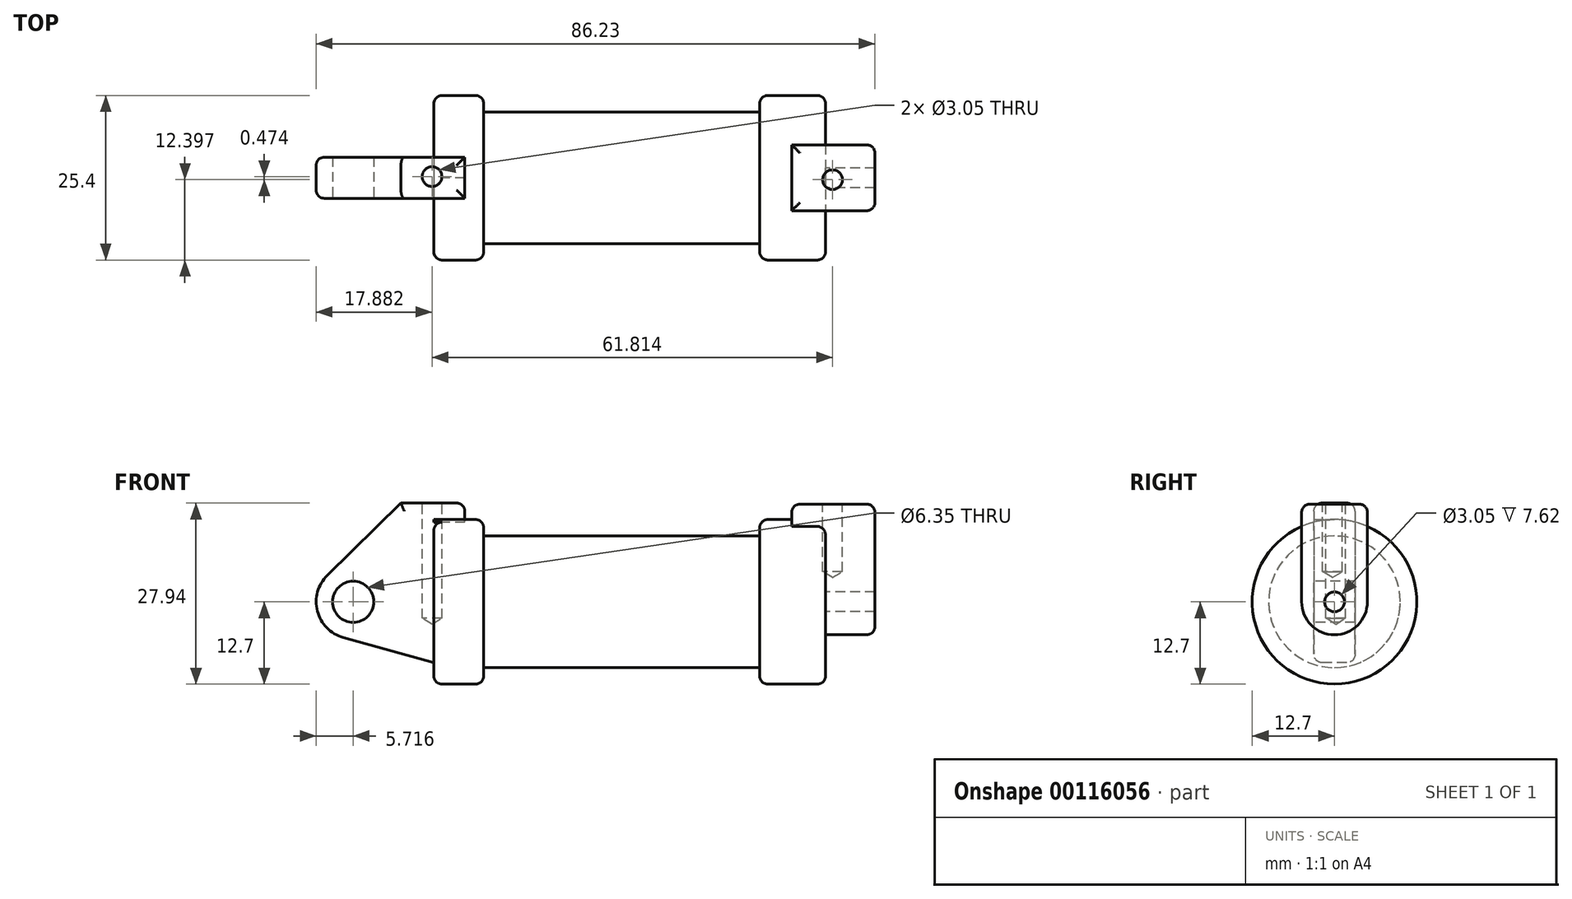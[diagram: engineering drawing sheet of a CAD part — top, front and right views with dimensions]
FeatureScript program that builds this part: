
annotation { "Feature Type Name" : "Feature", "Feature Type Description" : "" }
export const myFeature = defineFeature(function(context is Context, id is Id, definition is map)
    precondition{}
    {
        {
            var Q0;
            Q0=qCreatedBy(makeId("Front.planeOp"),FACE);
            var sketch = newSketch(context, id + "F0", { "sketchPlane" : qUnion([Q0])});
            skLineSegment(sketch, "E0", {"start": v(0, 0) * mm, "end": v(0, 12.7) * mm});
            skLineSegment(sketch, "E1", {"start": v(0, 12.7) * mm, "end": v(10.16, 12.7) * mm});
            skLineSegment(sketch, "E2", {"start": v(10.16, 12.7) * mm, "end": v(10.16, 10.16) * mm});
            skLineSegment(sketch, "E3", {"start": v(10.16, 10.16) * mm, "end": v(56.13, 10.16) * mm});
            skLineSegment(sketch, "E4", {"start": v(56.13, 10.16) * mm, "end": v(56.13, 12.7) * mm});
            skLineSegment(sketch, "E5", {"start": v(56.13, 12.7) * mm, "end": v(66.3, 12.7) * mm});
            skLineSegment(sketch, "E6", {"start": v(66.3, 12.7) * mm, "end": v(66.3, 0) * mm});
            skLineSegment(sketch, "E7", {"start": v(66.3, 0) * mm, "end": v(0, 0) * mm});
            skLineSegment(sketch, "E8", {"start": v(5.84, 15.24) * mm, "end": v(0.76, 15.24) * mm});
            skLineSegment(sketch, "E9", {"start": v(0.76, 15.24) * mm, "end": v(-10.6, 4.08) * mm});
            skLineSegment(sketch, "E10", {"start": v(0, 0) * mm, "end": v(-6.6, 0) * mm});
            skCircle(sketch, "E11", {"center": v(-6.6, 0) * mm, "radius": 5.72 * mm});
            skCircle(sketch, "E12", {"center": v(-6.6, 0) * mm, "radius": 3.18 * mm});
            skLineSegment(sketch, "E13", {"start": v(5.84, 15.24) * mm, "end": v(5.84, -9.4) * mm});
            skLineSegment(sketch, "E14", {"start": v(5.84, -9.4) * mm, "end": v(-8.14, -5.5) * mm});
            skSolve(sketch);
        }
        {
            var Q0;
            {var subQ0=sQuery(id+"F0.wireOp",EDGE,"E2");Q0=makeQuery(id+"F0.imprint","IMPRINT",FACE,{"disambiguationData":[TD([[makeQuery(id+"F0.imprint","IMPRINT",EDGE,{"derivedFrom":subQ0}),-1.0]])]});}
            var Q1;
            Q1=sQuery(id+"F0.wireOp",EDGE,"E7");
            revolve(context, id + "F1", {"entities" : qUnion([Q0]), "axis" : qUnion([Q1]), "revolveType" : RevolveType.FULL});
        }
        {
            var Q0;
            {var subQ0=sQuery(id+"F0.wireOp",EDGE,"E14");Q0=makeQuery(id+"F0.imprint","IMPRINT",FACE,{"disambiguationData":[TD([[makeQuery(id+"F0.imprint","IMPRINT",EDGE,{"derivedFrom":subQ0}),-1.0]])]});}
            var Q1;
            {var subQ0=sQuery(id+"F0.wireOp",EDGE,"E0");Q1=makeQuery(id+"F0.imprint","IMPRINT",FACE,{"disambiguationData":[TD([[makeQuery(id+"F0.imprint","IMPRINT",EDGE,{"derivedFrom":subQ0}),-1.0]])]});}
            var Q2;
            {var subQ4=sQuery(id+"F0.wireOp",EDGE,"E12");Q2=makeQuery(id+"F0.imprint","IMPRINT",FACE,{"disambiguationData":[TD([[makeQuery(id+"F0.imprint","IMPRINT",EDGE,{"derivedFrom":subQ4}),-1.0]])]});}
            var Q3;
            {var subQ3=sQuery(id+"F0.wireOp",EDGE,"E0");Q3=makeQuery(id+"F0.imprint","IMPRINT",FACE,{"disambiguationData":[TD([[makeQuery(id+"F0.imprint","IMPRINT",EDGE,{"derivedFrom":subQ3}),1.0]])]});}
            extrude(context, id + "F2", {"entities" : qUnion([Q0, Q1, Q2, Q3]), "operationType" : NewBodyOperationType.ADD, "oppositeDirection" : true, "depth" : 3.17 * mm});
        }
        {
            var Q0;
            {var subQ3=sQuery(id+"F0.wireOp",EDGE,"E0");Q0=makeQuery(id+"F0.imprint","IMPRINT",FACE,{"disambiguationData":[TD([[makeQuery(id+"F0.imprint","IMPRINT",EDGE,{"derivedFrom":subQ3}),1.0]])]});}
            var Q1;
            {var subQ0=sQuery(id+"F0.wireOp",EDGE,"E14");Q1=makeQuery(id+"F0.imprint","IMPRINT",FACE,{"disambiguationData":[TD([[makeQuery(id+"F0.imprint","IMPRINT",EDGE,{"derivedFrom":subQ0}),-1.0]])]});}
            var Q2;
            {var subQ4=sQuery(id+"F0.wireOp",EDGE,"E12");Q2=makeQuery(id+"F0.imprint","IMPRINT",FACE,{"disambiguationData":[TD([[makeQuery(id+"F0.imprint","IMPRINT",EDGE,{"derivedFrom":subQ4}),-1.0]])]});}
            extrude(context, id + "F3", {"entities" : qUnion([Q0, Q1, Q2]), "operationType" : NewBodyOperationType.ADD, "depth" : 3.17 * mm});
        }
        {
            var Q0;
            Q0=makeQuery(id+"F1.opRevolve","SWEPT_FACE",FACE,{"disambiguationData":[OSD([sQuery(id+"F0.wireOp",EDGE,"E2")])]});
            extrude(context, id + "F4", {"entities" : qUnion([Q0]), "operationType" : NewBodyOperationType.ADD, "depth" : 3.38 * mm});
        }
        {
            var Q0;
            {var subQ0=sQuery(id+"F0.wireOp",EDGE,"E13");Q0=makeQuery(id+"F3.boolean.opBoolean","MERGE",FACE,{"derivedFrom":[makeQuery(id+"F2.opExtrude","SWEPT_FACE",FACE,{"disambiguationData":[OSD([subQ0])]}),makeQuery(id+"F3.opExtrude","SWEPT_FACE",FACE,{"disambiguationData":[OSD([subQ0]),TDD([makeQuery(id+"F0.imprint","IMPRINT",EDGE,{"disambiguationData":[TD([[makeQuery(id+"F0.imprint","INTERSECT",VERTEX,{"derivedFrom":[sQuery(id+"F0.wireOp",EDGE,"E8"),subQ0]}),-1.0]])],"derivedFrom":subQ0})])]})]});}
            extrude(context, id + "F5", {"entities" : qUnion([Q0]), "operationType" : NewBodyOperationType.ADD, "depth" : 4.8 * mm});
        }
        {
            var Q0;
            {var subQ0=sQuery(id+"F0.wireOp",EDGE,"E0");Q0=makeQuery(id+"F0.imprint","IMPRINT",FACE,{"disambiguationData":[TD([[makeQuery(id+"F0.imprint","IMPRINT",EDGE,{"derivedFrom":subQ0}),-1.0]])]});}
            extrude(context, id + "F6", {"entities" : qUnion([Q0]), "operationType" : NewBodyOperationType.ADD, "depth" : 3.17 * mm});
        }
        {
            var Q0;
            Q0=makeQuery(id+"F1.opRevolve","SWEPT_FACE",FACE,{"disambiguationData":[OSD([sQuery(id+"F0.wireOp",EDGE,"E6")])]});
            var sketch = newSketch(context, id + "F7", { "sketchPlane" : qUnion([Q0])});
            skCircle(sketch, "E15", {"center": v(0, 0) * mm, "radius": 1.52 * mm});
            skCircle(sketch, "E16", {"center": v(0, 0) * mm, "radius": 5.08 * mm});
            skLineSegment(sketch, "E17", {"start": v(-5.08, 0) * mm, "end": v(-5.08, 15.08) * mm});
            skLineSegment(sketch, "E18", {"start": v(5.08, 0) * mm, "end": v(5.08, 15.08) * mm});
            skLineSegment(sketch, "E19", {"start": v(5.08, 15.08) * mm, "end": v(-5.08, 15.08) * mm});
            skSolve(sketch);
        }
        {
            var Q0;
            Q0=makeQuery(id+"F7.imprint","IMPRINT",FACE,{"disambiguationData":[TD([[makeQuery(id+"F7.imprint","IMPRINT",EDGE,{"derivedFrom":sQuery(id+"F7.wireOp",EDGE,"E15")}),-1.0]])]});
            var Q1;
            {var subQ0=sQuery(id+"F7.wireOp",EDGE,"E17");var subQ1=sQuery(id+"F7.wireOp",EDGE,"E16");var subQ2=makeQuery(id+"F7.imprint","INTERSECT",VERTEX,{"derivedFrom":[subQ1,subQ0]});Q1=makeQuery(id+"F7.imprint","IMPRINT",FACE,{"disambiguationData":[TD([[makeQuery(id+"F7.imprint","IMPRINT",EDGE,{"disambiguationData":[TD([[subQ2,1.0]])],"derivedFrom":subQ1}),-1.0]])]});}
            var Q2;
            {var subQ0=sQuery(id+"F7.wireOp",EDGE,"E19");Q2=makeQuery(id+"F7.imprint","IMPRINT",FACE,{"disambiguationData":[TD([[makeQuery(id+"F7.imprint","IMPRINT",EDGE,{"derivedFrom":subQ0}),1.0]])]});}
            extrude(context, id + "F8", {"entities" : qUnion([Q0, Q1, Q2]), "operationType" : NewBodyOperationType.ADD, "depth" : 7.62 * mm});
        }
        {
            var Q0;
            Q0=makeQuery(id+"F8.opExtrude","CAP_FACE",FACE,{"disambiguationData":[OSD([sQuery(id+"F7.wireOp",EDGE,"E15"),sQuery(id+"F7.wireOp",EDGE,"E16"),sQuery(id+"F7.wireOp",EDGE,"E17"),sQuery(id+"F7.wireOp",EDGE,"E18"),sQuery(id+"F7.wireOp",EDGE,"E19")])],"isStart":true});
            extrude(context, id + "F9", {"entities" : qUnion([Q0]), "operationType" : NewBodyOperationType.ADD, "depth" : 5.2 * mm});
        }
        {
            var Q0;
            {var subQ0=sQuery(id+"F7.wireOp",EDGE,"E19");Q0=makeQuery(id+"F9.boolean.opBoolean","MERGE",FACE,{"derivedFrom":[makeQuery(id+"F8.opExtrude","SWEPT_FACE",FACE,{"disambiguationData":[OSD([subQ0])]}),makeQuery(id+"F9.opExtrude","SWEPT_FACE",FACE,{"disambiguationData":[OSD([subQ0])]})]});}
            var sketch = newSketch(context, id + "F10", { "sketchPlane" : qUnion([Q0])});
            skCircle(sketch, "E20", {"center": v(67.38, -0.3) * mm, "radius": 1.52 * mm});
            skSolve(sketch);
        }
        {
            var Q0;
            {var subQ0=sQuery(id+"F0.wireOp",EDGE,"E8");Q0=makeQuery(id+"F5.boolean.opBoolean","MERGE",FACE,{"derivedFrom":[makeQuery(id+"F3.boolean.opBoolean","MERGE",FACE,{"derivedFrom":[makeQuery(id+"F2.opExtrude","SWEPT_FACE",FACE,{"disambiguationData":[OSD([subQ0])]}),makeQuery(id+"F3.opExtrude","SWEPT_FACE",FACE,{"disambiguationData":[OSD([subQ0])]})]}),makeQuery(id+"F5.opExtrude","SWEPT_FACE",FACE,{"disambiguationData":[OSD([subQ0,sQuery(id+"F0.wireOp",EDGE,"E13")])]})]});}
            var sketch = newSketch(context, id + "F11", { "sketchPlane" : qUnion([Q0])});
            skCircle(sketch, "E21", {"center": v(5.56, 0.17) * mm, "radius": 1.52 * mm});
            skSolve(sketch);
        }
        {
            var Q0;
            Q0=sQuery(id+"F11.wireOp",VERTEX,"E21.center");
            var Q1;
            Q1=makeQuery(id+"F1.opRevolve","SWEPT_BODY",BODY,{"disambiguationData":[OSD([sQuery(id+"F0.wireOp",EDGE,"E1"),sQuery(id+"F0.wireOp",EDGE,"E2"),sQuery(id+"F0.wireOp",EDGE,"E3"),sQuery(id+"F0.wireOp",EDGE,"E4"),sQuery(id+"F0.wireOp",EDGE,"E5"),sQuery(id+"F0.wireOp",EDGE,"E6"),sQuery(id+"F0.wireOp",EDGE,"E7"),sQuery(id+"F0.wireOp",EDGE,"E13")])]});
            hole(context, id + "F12", {"style" : HoleStyle.SIMPLE, "endStyle" : HoleEndStyle.BLIND, "holeDiameter" : 3.05 * mm, "holeDepth" : 17.78 * mm, "locations" : qUnion([Q0]), "scope" : qUnion([Q1])});
        }
        {
            var Q0;
            Q0=sQuery(id+"F10.wireOp",VERTEX,"E20.center");
            var Q1;
            Q1=makeQuery(id+"F1.opRevolve","SWEPT_BODY",BODY,{"disambiguationData":[OSD([sQuery(id+"F0.wireOp",EDGE,"E1"),sQuery(id+"F0.wireOp",EDGE,"E2"),sQuery(id+"F0.wireOp",EDGE,"E3"),sQuery(id+"F0.wireOp",EDGE,"E4"),sQuery(id+"F0.wireOp",EDGE,"E5"),sQuery(id+"F0.wireOp",EDGE,"E6"),sQuery(id+"F0.wireOp",EDGE,"E7"),sQuery(id+"F0.wireOp",EDGE,"E13")])]});
            hole(context, id + "F13", {"style" : HoleStyle.SIMPLE, "endStyle" : HoleEndStyle.BLIND, "holeDiameter" : 3.05 * mm, "holeDepth" : 10.4 * mm, "locations" : qUnion([Q0]), "scope" : qUnion([Q1])});
        }
        {
            var Q0;
            Q0=makeQuery(id+"F3.opExtrude","CAP_EDGE",EDGE,{"disambiguationData":[OSD([sQuery(id+"F0.wireOp",EDGE,"E9")])],"isStart":false});
            var Q1;
            Q1=makeQuery(id+"F2.opExtrude","CAP_EDGE",EDGE,{"disambiguationData":[OSD([sQuery(id+"F0.wireOp",EDGE,"E9")])],"isStart":false});
            var Q2;
            {var subQ0=sQuery(id+"F0.wireOp",EDGE,"E1");var subQ2=sQuery(id+"F0.wireOp",EDGE,"E13");var subQ3=makeQuery(id+"F1.opRevolve","SWEPT_FACE",FACE,{"disambiguationData":[OSD([subQ2])]});Q2=makeQuery(id+"F6.boolean.opBoolean","SPLIT",EDGE,{"disambiguationData":[topologyDisambiguationEdgeConnected([subQ3])],"derivedFrom":makeQuery(id+"F2.boolean.opBoolean","SPLIT",EDGE,{"disambiguationData":[topologyDisambiguationEdgeConnected([subQ3])],"derivedFrom":makeQuery(id+"F1.opRevolve","SWEPT_EDGE",EDGE,{"disambiguationData":[OSD([subQ0,subQ2])]})})});}
            var Q3;
            Q3=makeQuery(id+"F4.opExtrude","CAP_EDGE",EDGE,{"disambiguationData":[OSD([sQuery(id+"F0.wireOp",EDGE,"E1"),sQuery(id+"F0.wireOp",EDGE,"E2")])],"isStart":false});
            var Q4;
            {var subQ0=sQuery(id+"F0.wireOp",EDGE,"E13");var subQ1=sQuery(id+"F0.wireOp",EDGE,"E8");Q4=makeQuery(id+"F5.boolean.opBoolean","MERGE",EDGE,{"derivedFrom":[makeQuery(id+"F2.opExtrude","CAP_EDGE",EDGE,{"disambiguationData":[OSD([subQ1])],"isStart":false}),makeQuery(id+"F5.opExtrude","SWEPT_EDGE",EDGE,{"disambiguationData":[OSD([subQ1,subQ0]),TDD([makeQuery(id+"F2.opExtrude","CAP_VERTEX",VERTEX,{"disambiguationData":[OSD([subQ1,subQ0])],"isStart":false})])]})]});}
            var Q5;
            {var subQ0=sQuery(id+"F0.wireOp",EDGE,"E13");var subQ1=sQuery(id+"F0.wireOp",EDGE,"E8");Q5=makeQuery(id+"F5.boolean.opBoolean","MERGE",EDGE,{"derivedFrom":[makeQuery(id+"F3.opExtrude","CAP_EDGE",EDGE,{"disambiguationData":[OSD([subQ1])],"isStart":false}),makeQuery(id+"F5.opExtrude","SWEPT_EDGE",EDGE,{"disambiguationData":[OSD([subQ1,subQ0]),TDD([makeQuery(id+"F3.opExtrude","CAP_VERTEX",VERTEX,{"disambiguationData":[OSD([subQ1,subQ0])],"isStart":false})])]})]});}
            var Q6;
            Q6=makeQuery(id+"F5.opExtrude","CAP_EDGE",EDGE,{"disambiguationData":[OSD([sQuery(id+"F0.wireOp",EDGE,"E8"),sQuery(id+"F0.wireOp",EDGE,"E13")])],"isStart":false});
            var Q7;
            Q7=makeQuery(id+"F1.opRevolve","SWEPT_EDGE",EDGE,{"disambiguationData":[OSD([sQuery(id+"F0.wireOp",EDGE,"E4"),sQuery(id+"F0.wireOp",EDGE,"E5")])]});
            var Q8;
            {var subQ0=sQuery(id+"F0.wireOp",EDGE,"E5");var subQ1=sQuery(id+"F0.wireOp",EDGE,"E6");Q8=makeQuery(id+"F8.boolean.opBoolean","SPLIT",EDGE,{"disambiguationData":[topologyDisambiguationEdgeConnected([makeQuery(id+"F1.opRevolve","SWEPT_FACE",FACE,{"disambiguationData":[OSD([subQ1])]})])],"derivedFrom":makeQuery(id+"F1.opRevolve","SWEPT_EDGE",EDGE,{"disambiguationData":[OSD([subQ0,subQ1])]})});}
            var Q9;
            {var subQ0=sQuery(id+"F7.wireOp",EDGE,"E19");var subQ1=sQuery(id+"F7.wireOp",EDGE,"E17");Q9=makeQuery(id+"F9.boolean.opBoolean","MERGE",EDGE,{"derivedFrom":[makeQuery(id+"F8.opExtrude","SWEPT_EDGE",EDGE,{"disambiguationData":[OSD([subQ1,subQ0])]}),makeQuery(id+"F9.opExtrude","SWEPT_EDGE",EDGE,{"disambiguationData":[OSD([subQ1,subQ0])]})]});}
            var Q10;
            {var subQ0=sQuery(id+"F7.wireOp",EDGE,"E19");var subQ1=sQuery(id+"F7.wireOp",EDGE,"E18");Q10=makeQuery(id+"F9.boolean.opBoolean","MERGE",EDGE,{"derivedFrom":[makeQuery(id+"F8.opExtrude","SWEPT_EDGE",EDGE,{"disambiguationData":[OSD([subQ1,subQ0])]}),makeQuery(id+"F9.opExtrude","SWEPT_EDGE",EDGE,{"disambiguationData":[OSD([subQ1,subQ0])]})]});}
            var Q11;
            Q11=makeQuery(id+"F8.opExtrude","CAP_EDGE",EDGE,{"disambiguationData":[OSD([sQuery(id+"F7.wireOp",EDGE,"E18")])],"isStart":false});
            var Q12;
            Q12=makeQuery(id+"F9.opExtrude","CAP_EDGE",EDGE,{"disambiguationData":[OSD([sQuery(id+"F7.wireOp",EDGE,"E19")])],"isStart":false});
            var Q13;
            {var subQ0=sQuery(id+"F0.wireOp",EDGE,"E1");var subQ1=sQuery(id+"F0.wireOp",EDGE,"E13");Q13=makeQuery(id+"F5.opExtrude","CAP_EDGE",EDGE,{"disambiguationData":[OSD([subQ0,subQ1]),TDD([makeQuery(id+"F2.boolean.opBoolean","SPLIT",EDGE,{"disambiguationData":[topologyDisambiguationEdgeConnected([makeQuery(id+"F2.opExtrude","SWEPT_FACE",FACE,{"disambiguationData":[OSD([subQ1])]})])],"derivedFrom":makeQuery(id+"F1.opRevolve","SWEPT_EDGE",EDGE,{"disambiguationData":[OSD([subQ0,subQ1])]})})])],"isStart":false});}
            var Q14;
            Q14=makeQuery(id+"F8.opExtrude","CAP_EDGE",EDGE,{"disambiguationData":[OSD([sQuery(id+"F7.wireOp",EDGE,"E19")])],"isStart":false});
            var Q15;
            {var subQ0=sQuery(id+"F7.wireOp",EDGE,"E17");Q15=makeQuery(id+"F8.boolean.opBoolean","SPLIT",EDGE,{"disambiguationData":[topologyDisambiguationEdgeConnected([makeQuery(id+"F1.opRevolve","SWEPT_FACE",FACE,{"disambiguationData":[OSD([sQuery(id+"F0.wireOp",EDGE,"E6")])]})])],"derivedFrom":makeQuery(id+"F8.opExtrude","CAP_EDGE",EDGE,{"disambiguationData":[OSD([subQ0])],"isStart":true})});}
            fillet(context, id + "F14", {"entities" : qUnion([Q0, Q1, Q2, Q3, Q4, Q5, Q6, Q7, Q8, Q9, Q10, Q11, Q12, Q13, Q14, Q15]), "radius" : 1.27 * mm, "tangentPropagation" : true, "allowEdgeOverflow" : false});
        }
    });
